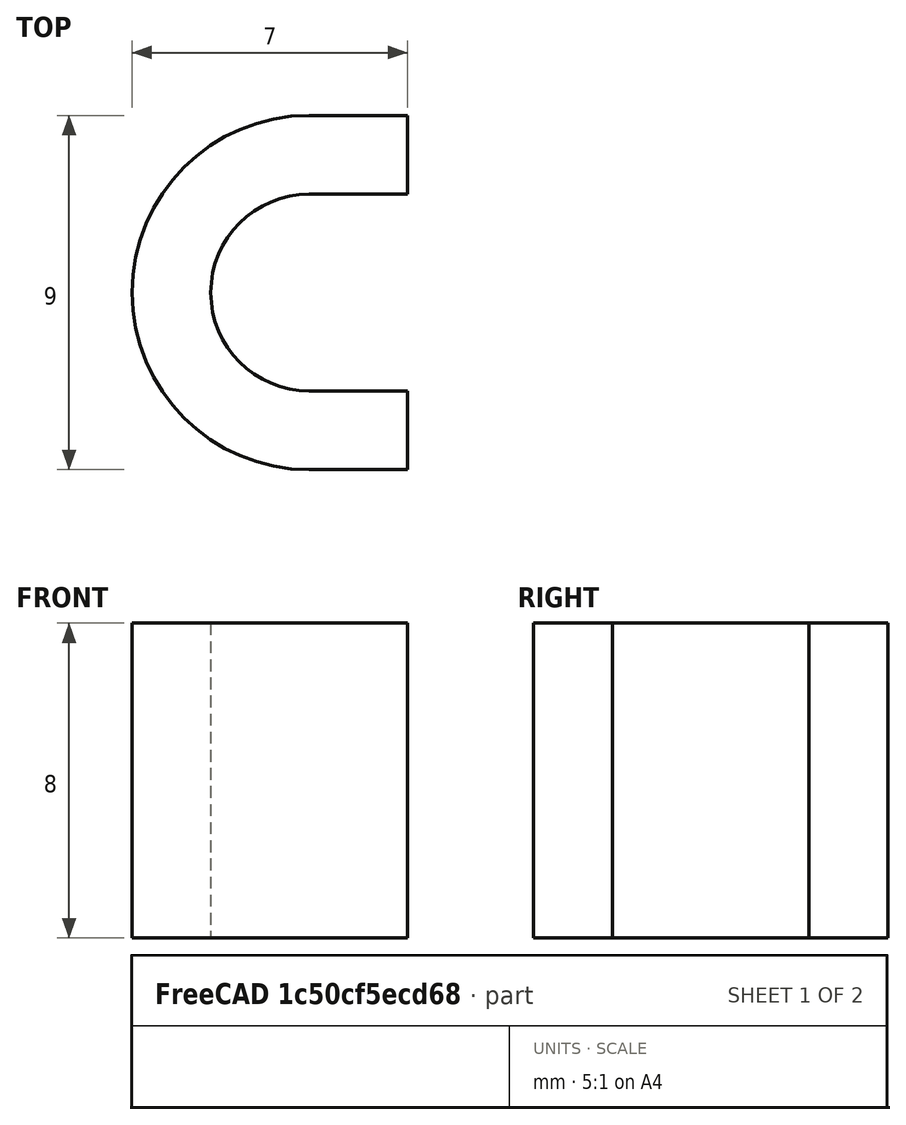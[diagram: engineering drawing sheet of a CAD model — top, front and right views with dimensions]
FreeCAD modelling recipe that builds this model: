
FCSTD DOCUMENT  (FreeCAD 0.16R6706 (Git))
Label: CapacitorConnectionCover
License: All rights reserved
LicenseURL: http://en.wikipedia.org/wiki/All_rights_reserved
objects: Sketcher::SketchObject×1, PartDesign::Pad×1
note: 3 computed .brp shape members not serialized (recipe doc carries the construction recipe); baked Part::Feature solids carry a one-line shape summary decoded from their .brp

FEATURE [Sketcher::SketchObject] Sketch
  sketch-geometry (12):
    g0: ArcOfCircle CenterX=0 CenterY=0 CenterZ=0 NormalX=0 NormalY=0 NormalZ=1 Radius=2.5 StartAngle=1.5708 EndAngle=4.71239
    g1: ArcOfCircle CenterX=0 CenterY=0 CenterZ=0 NormalX=0 NormalY=0 NormalZ=1 Radius=4.5 StartAngle=1.5708 EndAngle=4.71239
    g2: LineSegment StartX=0 StartY=4.5 StartZ=0 EndX=2.5 EndY=4.5 EndZ=0
    g3: LineSegment StartX=2.5 StartY=4.5 StartZ=0 EndX=2.5 EndY=2.5 EndZ=0
    g4: LineSegment StartX=2.5 StartY=2.5 StartZ=0 EndX=0 EndY=2.5 EndZ=0
    g5: LineSegment StartX=0 StartY=-2.5 StartZ=0 EndX=2.5 EndY=-2.5 EndZ=0
    g6: LineSegment StartX=2.5 StartY=-2.5 StartZ=0 EndX=2.5 EndY=-4.5 EndZ=0
    g7: LineSegment StartX=2.5 StartY=-4.5 StartZ=0 EndX=0 EndY=-4.5 EndZ=0
    g8: LineSegment [constr] StartX=2.5 StartY=2.5 StartZ=0 EndX=2.5 EndY=-2.5 EndZ=0
    g9: LineSegment [constr] StartX=-2.5 StartY=4.5 StartZ=0 EndX=-2.5 EndY=-4.5 EndZ=0
    g10: LineSegment [constr] StartX=-2.5 StartY=-4.5 StartZ=0 EndX=0 EndY=-4.5 EndZ=0
    g11: LineSegment [constr] StartX=-2.5 StartY=4.5 StartZ=0 EndX=0 EndY=4.5 EndZ=0
  constraints (32):
    c: Coincident(g0,g-1)
    c: PointOnObject(g0,g-2)
    c: PointOnObject(g0,g-2)
    c: Coincident(g1,g-1)
    c: PointOnObject(g1,g-2)
    c: PointOnObject(g1,g-2)
    c: Tangent(g1,g2) = 1.5708
    c: Coincident(g2,g3)
    c: Vertical(g3)
    c: Coincident(g3,g4)
    c: Coincident(g4,g0)
    c: Horizontal(g4)
    c: Tangent(g0,g5) = -1.5708
    c: Coincident(g5,g6)
    c: Vertical(g6)
    c: Coincident(g6,g7)
    c: Coincident(g7,g1)
    c: Horizontal(g7)
    c: Coincident(g8,g3)
    c: Coincident(g8,g5)
    c: Vertical(g8)
    c: DistanceY(g3,g2) = 2
    c: Vertical(g9)
    c: Tangent(g9,g0)
    c: Coincident(g10,g9)
    c: Horizontal(g10)
    c: Coincident(g10,g1)
    c: Equal(g10,g7)
    c: Coincident(g11,g1)
    c: Coincident(g11,g9)
    c: Horizontal(g11)
    c: DistanceY(g5,g3) = 5
FEATURE [PartDesign::Pad] Pad
  Length = 8
  Length2 = 100
  Sketch = -> Sketch
  Type = 0
